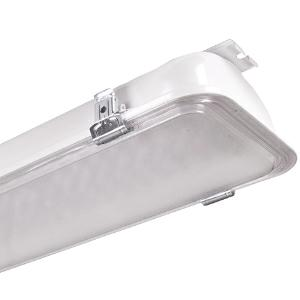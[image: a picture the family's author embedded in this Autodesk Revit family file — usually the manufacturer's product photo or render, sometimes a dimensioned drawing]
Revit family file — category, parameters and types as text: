
# Revit family: 3f_filippi_-_beta_235_75_pc_medio_3f_filippi_-_52553_-_beta_235_led_751x60_medio_l1565
name_source: partatom
category: Lighting Fixtures
units: mm (PartAtom-declared; Revit-internal decimal feet)

## family parameters
Cut with Voids When Loaded = No
Host = Face
Light Source = No
Part Type = Normal
Room Calculation Point = No
Round Connector Dimension = Use Diameter
Shared = No

## types (1)
- 3F Filippi - Beta 235 75 PC Medio (1 x LED, 9781 lm, 65 W, 4000 K)
    Apparent Load = 65 VA
    Approval mark = CE
    CIE Flux Codes = 68 91 99 100 100
    Color Rendering = 80
    Color Temperature = 4000 K
    Control Gear = Electronic ballast
    Default Elevation = 1800 mm
    Description = ILLUMINOTECHNICAL
Luminous efficiency 100% (DLOR 99%, ULOR 1%).
Initial luminous flux of the luminaire 9781 lm.
Medium symmetric distribution.
Installation Interdistance Transv.D = 1.16 x hu - Long.D = 1.16 x hu.
Average luminance <3000 cd/m² for radial angles >65°.
Tabular UGR (CIE 117 - 4H-8H; S=0.25H; 70/50/20): RUG 18.4 - 18.8.
Beam angle: 76° - 76°.
Luminous efficacy 150 lm/W.
Lifetime (L93/B10): 30000 h. (tq+25°C)
Lifetime (L90/B10): 50000 h. (tq+25°C)
Lifetime (L85/B10): 80000 h. (tq+25°C)
Lifetime (L80/B10): 100000 h. (tq+25°C)
Lifetime (L85/B10): 50000 h. (tq+45°C)
Sudden decreased luminous flux after 50000 hours: 0% (C0).
Photobiological safety in compliance with IEC/TR 62778: RG0 risk exempt, (IEC 62471).
In compliance with IEC/EN 62722-2-1 - IEC/EN 62717 standards.

SOURCE
Linear LED module 60W/840.
Energy efficiency class (UE 2019/2020 - UE 2019/2015): C.
CIE 13.3 Colour rendering index: CRI >80 (R9 <50%).
IES TM-30 Fidelity Index: Rf = 84 Rg = 95.
CCT nominal colour temperature 4000 K.
Colour initial tolerance (MacAdam): SDCM 3.

MECHANICAL
Single-piece housing in pressed steel, powder-coated in white epoxy-polyester.
Polycarbonate screen etched internally, V2 self-extinguishing, UV stabilised, injection moulded.
Ecologic anti-aging injected sealing gasket.
Oversized gear-tray reflector unit in highly reflective white painted hot-galvanised steel.
Methacrylate (PMMA) lenses with external flat surface.
Galvanised steel snap-lock clips for diffuser mounting (safety n° 4 per fixture).
Luminaire with limited surface temperature. - D - (EN 60598-2-24)
Dimensions: 1565x235 mm, height 107 mm. Weight 7.75 kg.
IP65 protection degree.
Mechanical strength to impacts IK09 (10 joule).
Glow-wire test resistance 850°C.

ELECTRICAL
Halogen Free electronic wiring 230V-50/60Hz, power factor 0.95, THD <25%, constant output current, class I, 1 driver.
Power of the luminaire 65 W.
ENEC - CE.
Flicker: <4%.
Luminaire compliant with EN 60598-2-22 for power supply from a centralised emergency system CPSS (Central Power Supply System), not incorporated in the luminaire - high risk areas excluded. The default power and flux are 100% in AC and 100% in DC.
Ambient temperature from -20°C to +45°C.
Temperature class T6 max 85°C.
Quick connection via M20 3P connector with 9-13 mm tightening range.
Relative humidity UR: <85%.

INSTALLATION
Ceiling / Suspended / Wall.
All accessories dedicated to this product are available on the Catalog and on our website www.3F-Filippi.com.

APPLICATIONS
Suitable product for food production plants (HACCP), IFS (Food Version 6), BRC (GSFS Food Version 7).
Dry, dusty indoor environments, subject to occasional water splashes.
Industrial environments, warehouses, environments where security locks are required on all clips, e.g. prisons (on request).
Environments in which it is necessary a total protection against falling fragments (eg environments with foodstuffs or machines with moving parts or with extreme temperature changes), use luminaires with laminated glass.
Tempered glass is not immune to falling fragments from harmless and caused by shocks or exceptionally derived from the tempering process.

WARNING
Fixture not suitable for cold stores with an ambient temperature <0°C and/or relative humidity >85%.
Luminaire designed for disposal/recycling at end-of-life.
Replaceable (LED only) light source by a professional. Replaceable control gear by a professional.
    Height = 107 mm
    Lamp = 1 x LED
    Lamp Light Flux = 9781 lm
    Lamp Power = 65 W
    Lamp count = 1
    Length = 1565 mm
    Lifetime = 50000 h
    Luminous efficacy = 150 lm/W
    Manufacturer = 3F Filippi
    ModVariant = No
    Model = 3F Filippi - 52553 - Beta 235 LED 751x60 MEDIO L1565
    Mounting Place = Ceiling
    Mounting Type = Pendant
    Number of Poles = 1
    OnlyDefault = Yes
    Power Factor = 1
    Product Name = 3F Filippi - Beta 235 75 PC Medio
    Product group = pendant luminaire
    ProductGroupID = 9
    Protection Class = Protection class I
    Protection Degree = IP 65
    RLX_Detail_Level = 1
    RLX_Emergency_Light_Flux = 0 lm
    RLX_Emergency_Type = 0
    RLX_Emergency_Type_DB = No
    RlxData = <blob elided: 83261 chars, md5=39e45bb3>
    Socket = socket
    Standby Power = 0 W
    System Light Flux = 9781 lm
    System Power = 65 W
    Type Comments = Product without accessories
    Type Image = 3ffilippi_beta_235_led_75_l1565.jpg
    URL = http://relux.com
    VarID = ---
    Voltage = 0 V
    Weight = 0.00 kg
    Width = 235 mm

## geometry (parser evidence)
native form markers: Blend x4, Sweep x10
no freeform markers — native parametric forms only
